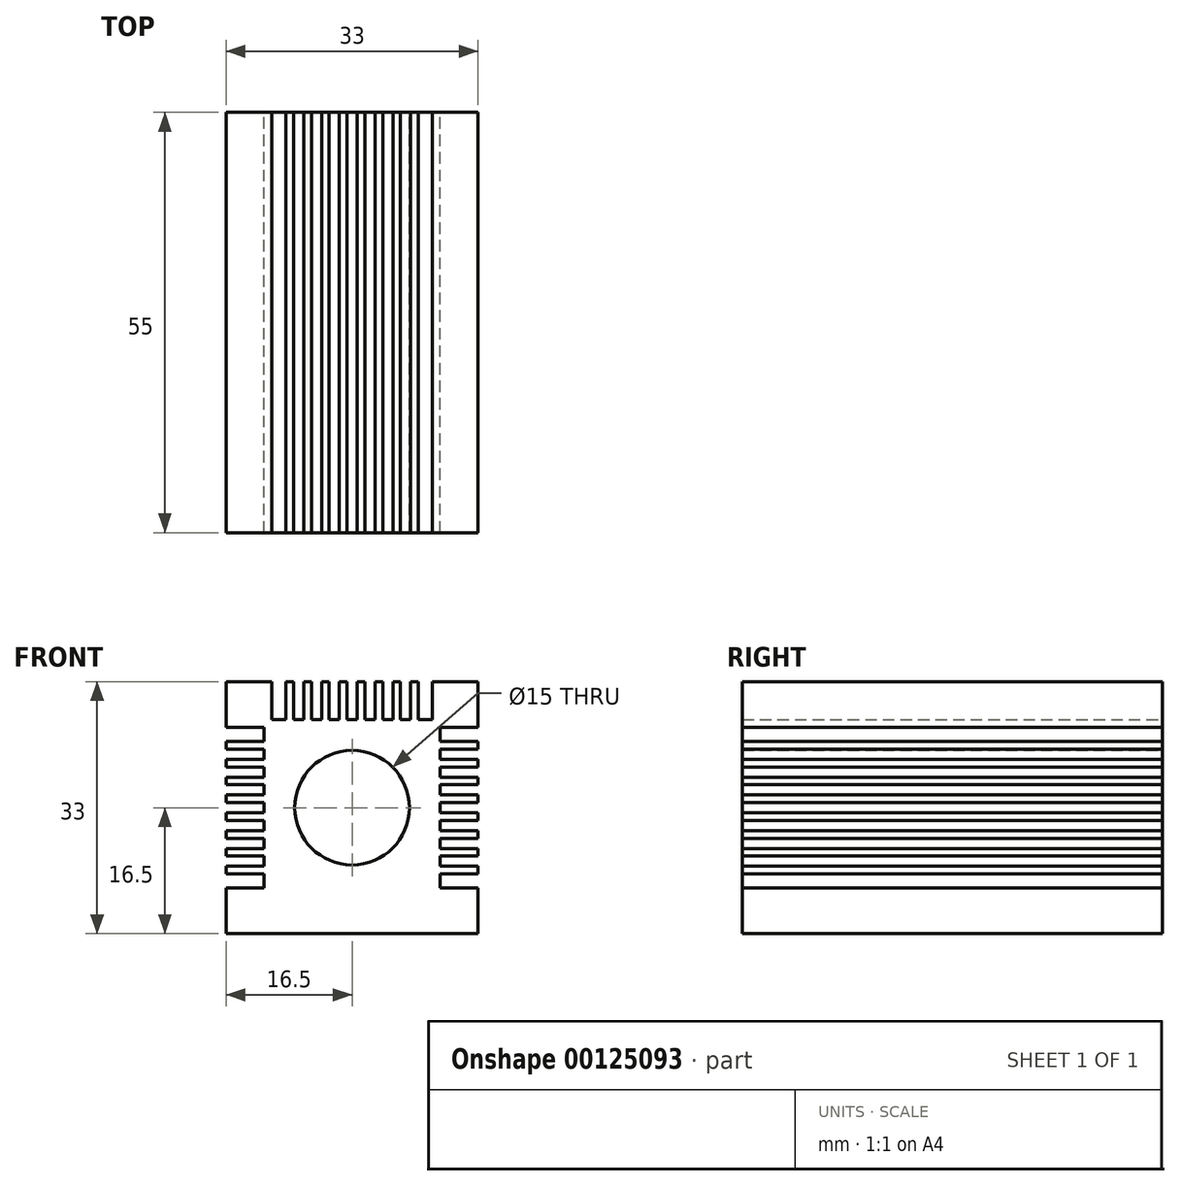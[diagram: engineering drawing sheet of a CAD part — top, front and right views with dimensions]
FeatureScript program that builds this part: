
annotation { "Feature Type Name" : "Feature", "Feature Type Description" : "" }
export const myFeature = defineFeature(function(context is Context, id is Id, definition is map)
    precondition{}
    {
        {
            var Q0;
            Q0=qCreatedBy(makeId("Front.planeOp"),FACE);
            var sketch = newSketch(context, id + "F0", { "sketchPlane" : qUnion([Q0])});
            skLineSegment(sketch, "E0.bottom", {"start": v(0, 0) * mm, "end": v(33, 0) * mm});
            skLineSegment(sketch, "E0.top", {"start": v(0, 33) * mm, "end": v(6, 33) * mm});
            skLineSegment(sketch, "E0.left", {"start": v(0, 0) * mm, "end": v(0, 6) * mm});
            skLineSegment(sketch, "E0.right", {"start": v(33, 0) * mm, "end": v(33, 6) * mm});
            skLineSegment(sketch, "E1", {"start": v(6, 33) * mm, "end": v(6, 28) * mm});
            skLineSegment(sketch, "E2.MirrorCS", {"start": v(27, 33) * mm, "end": v(27, 28) * mm});
            skLineSegment(sketch, "E3.MirrorCS", {"start": v(6, 28) * mm, "end": v(7.83, 28) * mm});
            skPoint(sketch, "E4.orphan", {"position": v(6, 0) * mm});
            skPoint(sketch, "E5.orphan", {"position": v(16.5, 0) * mm});
            skPoint(sketch, "E6.orphan", {"position": v(27, 0) * mm});
            skPoint(sketch, "E7.start.orphan", {"position": v(16.5, 33) * mm});
            skPoint(sketch, "E8.trimOffspring.end.orphan", {"position": v(33, 16.5) * mm});
            skPoint(sketch, "E9.start.orphan", {"position": v(0, 16.5) * mm});
            skLineSegment(sketch, "E10", {"start": v(7.83, 33) * mm, "end": v(7.83, 28) * mm});
            skLineSegment(sketch, "E11.MirrorCS", {"start": v(8.83, 33) * mm, "end": v(8.83, 28) * mm});
            skLineSegment(sketch, "E12.1.0.0", {"start": v(10.17, 33) * mm, "end": v(10.17, 28) * mm});
            skLineSegment(sketch, "E12.1.0.1", {"start": v(11.17, 33) * mm, "end": v(11.17, 28) * mm});
            skLineSegment(sketch, "E12.2.0.0", {"start": v(12.5, 33) * mm, "end": v(12.5, 28) * mm});
            skLineSegment(sketch, "E12.2.0.1", {"start": v(13.5, 33) * mm, "end": v(13.5, 28) * mm});
            skLineSegment(sketch, "E12.3.0.0", {"start": v(14.83, 33) * mm, "end": v(14.83, 28) * mm});
            skLineSegment(sketch, "E12.3.0.1", {"start": v(15.83, 33) * mm, "end": v(15.83, 28) * mm});
            skLineSegment(sketch, "E12.4.0.0", {"start": v(17.17, 33) * mm, "end": v(17.17, 28) * mm});
            skLineSegment(sketch, "E12.4.0.1", {"start": v(18.17, 33) * mm, "end": v(18.17, 28) * mm});
            skLineSegment(sketch, "E12.5.0.0", {"start": v(19.5, 33) * mm, "end": v(19.5, 28) * mm});
            skLineSegment(sketch, "E12.5.0.1", {"start": v(20.5, 33) * mm, "end": v(20.5, 28) * mm});
            skLineSegment(sketch, "E12.6.0.0", {"start": v(21.83, 33) * mm, "end": v(21.83, 28) * mm});
            skLineSegment(sketch, "E12.6.0.1", {"start": v(22.83, 33) * mm, "end": v(22.83, 28) * mm});
            skLineSegment(sketch, "E12.7.0.0", {"start": v(24.17, 33) * mm, "end": v(24.17, 28) * mm});
            skLineSegment(sketch, "E12.7.0.1", {"start": v(25.17, 33) * mm, "end": v(25.17, 28) * mm});
            skLineSegment(sketch, "E12.direction1", {"start": v(8.83, 28) * mm, "end": v(10.17, 28) * mm, "construction": true});
            skLineSegment(sketch, "E13.trimOffspring", {"start": v(7.83, 33) * mm, "end": v(8.83, 33) * mm});
            skLineSegment(sketch, "E14.trimOffspring", {"start": v(10.17, 33) * mm, "end": v(11.17, 33) * mm});
            skLineSegment(sketch, "E15.trimOffspring", {"start": v(12.5, 33) * mm, "end": v(13.5, 33) * mm});
            skLineSegment(sketch, "E16.trimOffspring", {"start": v(14.83, 33) * mm, "end": v(15.83, 33) * mm});
            skLineSegment(sketch, "E17.trimOffspring", {"start": v(17.17, 33) * mm, "end": v(18.17, 33) * mm});
            skLineSegment(sketch, "E18.trimOffspring", {"start": v(19.5, 33) * mm, "end": v(20.5, 33) * mm});
            skLineSegment(sketch, "E19.trimOffspring", {"start": v(21.83, 33) * mm, "end": v(22.83, 33) * mm});
            skLineSegment(sketch, "E20.trimOffspring", {"start": v(24.17, 33) * mm, "end": v(25.17, 33) * mm});
            skLineSegment(sketch, "E21.trimOffspring", {"start": v(27, 33) * mm, "end": v(33, 33) * mm});
            skLineSegment(sketch, "E22.MirrorCS", {"start": v(0, 18.17) * mm, "end": v(0, 17.17) * mm});
            skLineSegment(sketch, "E23.MirrorCS", {"start": v(0, 8.83) * mm, "end": v(0, 7.83) * mm});
            skLineSegment(sketch, "E24.MirrorCS", {"start": v(0, 22.83) * mm, "end": v(0, 21.83) * mm});
            skLineSegment(sketch, "E25.MirrorCS", {"start": v(0, 11.17) * mm, "end": v(0, 10.17) * mm});
            skLineSegment(sketch, "E26.MirrorCS", {"start": v(0, 13.5) * mm, "end": v(0, 12.5) * mm});
            skLineSegment(sketch, "E27.MirrorCS", {"start": v(0, 20.5) * mm, "end": v(0, 19.5) * mm});
            skLineSegment(sketch, "E28.MirrorCS", {"start": v(0, 25.17) * mm, "end": v(0, 24.17) * mm});
            skLineSegment(sketch, "E29.MirrorCS", {"start": v(0, 15.83) * mm, "end": v(0, 14.83) * mm});
            skLineSegment(sketch, "E30.MirrorCS", {"start": v(0, 6) * mm, "end": v(5, 6) * mm});
            skLineSegment(sketch, "E31.MirrorCS", {"start": v(0, 7.83) * mm, "end": v(5, 7.83) * mm});
            skLineSegment(sketch, "E32.MirrorCS", {"start": v(0, 27) * mm, "end": v(5, 27) * mm});
            skLineSegment(sketch, "E33.MirrorCS", {"start": v(0, 13.5) * mm, "end": v(5, 13.5) * mm});
            skLineSegment(sketch, "E34.MirrorCS", {"start": v(0, 18.17) * mm, "end": v(5, 18.17) * mm});
            skLineSegment(sketch, "E35.MirrorCS", {"start": v(0, 8.83) * mm, "end": v(5, 8.83) * mm});
            skLineSegment(sketch, "E36.MirrorCS", {"start": v(0, 21.83) * mm, "end": v(5, 21.83) * mm});
            skLineSegment(sketch, "E37.MirrorCS", {"start": v(0, 11.17) * mm, "end": v(5, 11.17) * mm});
            skLineSegment(sketch, "E38.MirrorCS", {"start": v(0, 22.83) * mm, "end": v(5, 22.83) * mm});
            skLineSegment(sketch, "E39.MirrorCS", {"start": v(0, 12.5) * mm, "end": v(5, 12.5) * mm});
            skLineSegment(sketch, "E40.MirrorCS", {"start": v(0, 15.83) * mm, "end": v(5, 15.83) * mm});
            skLineSegment(sketch, "E41.MirrorCS", {"start": v(0, 25.17) * mm, "end": v(5, 25.17) * mm});
            skLineSegment(sketch, "E42.MirrorCS", {"start": v(0, 20.5) * mm, "end": v(5, 20.5) * mm});
            skLineSegment(sketch, "E43.MirrorCS", {"start": v(0, 17.17) * mm, "end": v(5, 17.17) * mm});
            skLineSegment(sketch, "E44.MirrorCS", {"start": v(0, 19.5) * mm, "end": v(5, 19.5) * mm});
            skLineSegment(sketch, "E45.MirrorCS", {"start": v(0, 14.83) * mm, "end": v(5, 14.83) * mm});
            skLineSegment(sketch, "E46.MirrorCS", {"start": v(0, 24.17) * mm, "end": v(5, 24.17) * mm});
            skLineSegment(sketch, "E47.MirrorCS", {"start": v(0, 10.17) * mm, "end": v(5, 10.17) * mm});
            skLineSegment(sketch, "E48", {"start": v(5, 27) * mm, "end": v(5, 25.17) * mm});
            skLineSegment(sketch, "E49.trimOffspring", {"start": v(0, 27) * mm, "end": v(0, 33) * mm});
            skLineSegment(sketch, "E50.trimOffspring", {"start": v(0, 24.17) * mm, "end": v(0, 25.17) * mm});
            skLineSegment(sketch, "E51.trimOffspring", {"start": v(0, 21.83) * mm, "end": v(0, 22.83) * mm});
            skLineSegment(sketch, "E52.trimOffspring", {"start": v(0, 19.5) * mm, "end": v(0, 20.5) * mm});
            skLineSegment(sketch, "E53.trimOffspring", {"start": v(0, 7.83) * mm, "end": v(0, 8.83) * mm});
            skLineSegment(sketch, "E54.trimOffspring", {"start": v(0, 10.17) * mm, "end": v(0, 11.17) * mm});
            skLineSegment(sketch, "E55.trimOffspring", {"start": v(0, 12.5) * mm, "end": v(0, 13.5) * mm});
            skLineSegment(sketch, "E56.trimOffspring", {"start": v(0, 14.83) * mm, "end": v(0, 15.83) * mm});
            skLineSegment(sketch, "E57.trimOffspring", {"start": v(0, 17.17) * mm, "end": v(0, 18.17) * mm});
            skLineSegment(sketch, "E58.trimOffspring", {"start": v(25.17, 28) * mm, "end": v(27, 28) * mm});
            skLineSegment(sketch, "E59.trimOffspring", {"start": v(22.83, 28) * mm, "end": v(24.17, 28) * mm});
            skLineSegment(sketch, "E60.trimOffspring", {"start": v(20.5, 28) * mm, "end": v(21.83, 28) * mm});
            skLineSegment(sketch, "E61.trimOffspring", {"start": v(18.17, 28) * mm, "end": v(19.5, 28) * mm});
            skLineSegment(sketch, "E62.trimOffspring", {"start": v(15.83, 28) * mm, "end": v(17.17, 28) * mm});
            skLineSegment(sketch, "E63.trimOffspring", {"start": v(11.17, 28) * mm, "end": v(12.5, 28) * mm});
            skLineSegment(sketch, "E64.trimOffspring", {"start": v(8.83, 28) * mm, "end": v(10.17, 28) * mm});
            skLineSegment(sketch, "E65.trimOffspring", {"start": v(13.5, 28) * mm, "end": v(14.83, 28) * mm});
            skLineSegment(sketch, "E66.trimOffspring", {"start": v(5, 21.83) * mm, "end": v(5, 20.5) * mm});
            skLineSegment(sketch, "E67.trimOffspring", {"start": v(5, 24.17) * mm, "end": v(5, 22.83) * mm});
            skLineSegment(sketch, "E68.trimOffspring", {"start": v(5, 19.5) * mm, "end": v(5, 18.17) * mm});
            skLineSegment(sketch, "E69.trimOffspring", {"start": v(5, 10.17) * mm, "end": v(5, 8.83) * mm});
            skLineSegment(sketch, "E70.trimOffspring", {"start": v(5, 12.5) * mm, "end": v(5, 11.17) * mm});
            skLineSegment(sketch, "E71.trimOffspring", {"start": v(5, 7.83) * mm, "end": v(5, 6) * mm});
            skLineSegment(sketch, "E72.trimOffspring", {"start": v(5, 17.17) * mm, "end": v(5, 13.5) * mm});
            skLineSegment(sketch, "E73.MirrorCS", {"start": v(28, 8.83) * mm, "end": v(28, 10.17) * mm});
            skLineSegment(sketch, "E74.MirrorCS", {"start": v(28, 8.83) * mm, "end": v(28, 10.17) * mm, "construction": true});
            skLineSegment(sketch, "E75.MirrorCS", {"start": v(28, 18.17) * mm, "end": v(28, 19.5) * mm});
            skLineSegment(sketch, "E76.MirrorCS", {"start": v(28, 15.83) * mm, "end": v(28, 17.17) * mm});
            skLineSegment(sketch, "E77.MirrorCS", {"start": v(28, 11.17) * mm, "end": v(28, 12.5) * mm});
            skLineSegment(sketch, "E78.MirrorCS", {"start": v(33, 21.83) * mm, "end": v(33, 22.83) * mm});
            skLineSegment(sketch, "E79.MirrorCS", {"start": v(28, 25.17) * mm, "end": v(28, 27) * mm});
            skLineSegment(sketch, "E80.MirrorCS", {"start": v(33, 24.17) * mm, "end": v(33, 25.17) * mm});
            skLineSegment(sketch, "E81.MirrorCS", {"start": v(28, 6) * mm, "end": v(28, 7.83) * mm});
            skLineSegment(sketch, "E82.MirrorCS", {"start": v(33, 17.17) * mm, "end": v(33, 18.17) * mm});
            skLineSegment(sketch, "E83.MirrorCS", {"start": v(28, 20.5) * mm, "end": v(28, 21.83) * mm});
            skLineSegment(sketch, "E84.MirrorCS", {"start": v(33, 7.83) * mm, "end": v(33, 8.83) * mm});
            skLineSegment(sketch, "E85.MirrorCS", {"start": v(33, 12.5) * mm, "end": v(33, 13.5) * mm});
            skLineSegment(sketch, "E86.MirrorCS", {"start": v(28, 13.5) * mm, "end": v(28, 14.83) * mm});
            skLineSegment(sketch, "E87.MirrorCS", {"start": v(28, 22.83) * mm, "end": v(28, 24.17) * mm});
            skLineSegment(sketch, "E88.MirrorCS", {"start": v(33, 14.83) * mm, "end": v(33, 15.83) * mm});
            skLineSegment(sketch, "E89.MirrorCS", {"start": v(33, 10.17) * mm, "end": v(33, 11.17) * mm});
            skLineSegment(sketch, "E90.MirrorCS", {"start": v(33, 19.5) * mm, "end": v(33, 20.5) * mm});
            skLineSegment(sketch, "E91.MirrorCS", {"start": v(33, 20.5) * mm, "end": v(28, 20.5) * mm});
            skLineSegment(sketch, "E92.MirrorCS", {"start": v(33, 21.83) * mm, "end": v(28, 21.83) * mm});
            skLineSegment(sketch, "E93.MirrorCS", {"start": v(33, 19.5) * mm, "end": v(28, 19.5) * mm});
            skLineSegment(sketch, "E94.MirrorCS", {"start": v(33, 22.83) * mm, "end": v(28, 22.83) * mm});
            skLineSegment(sketch, "E95.MirrorCS", {"start": v(33, 24.17) * mm, "end": v(28, 24.17) * mm});
            skLineSegment(sketch, "E96.MirrorCS", {"start": v(33, 25.17) * mm, "end": v(28, 25.17) * mm});
            skLineSegment(sketch, "E97.MirrorCS", {"start": v(33, 14.83) * mm, "end": v(28, 14.83) * mm});
            skLineSegment(sketch, "E98.MirrorCS", {"start": v(33, 15.83) * mm, "end": v(28, 15.83) * mm});
            skLineSegment(sketch, "E99.MirrorCS", {"start": v(33, 17.17) * mm, "end": v(28, 17.17) * mm});
            skLineSegment(sketch, "E100.MirrorCS", {"start": v(33, 6) * mm, "end": v(28, 6) * mm});
            skLineSegment(sketch, "E101.MirrorCS", {"start": v(33, 27) * mm, "end": v(28, 27) * mm});
            skLineSegment(sketch, "E102.MirrorCS", {"start": v(33, 8.83) * mm, "end": v(28, 8.83) * mm});
            skLineSegment(sketch, "E103.MirrorCS", {"start": v(33, 10.17) * mm, "end": v(28, 10.17) * mm});
            skLineSegment(sketch, "E104.MirrorCS", {"start": v(33, 13.5) * mm, "end": v(28, 13.5) * mm});
            skLineSegment(sketch, "E105.MirrorCS", {"start": v(33, 11.17) * mm, "end": v(28, 11.17) * mm});
            skLineSegment(sketch, "E106.MirrorCS", {"start": v(33, 7.83) * mm, "end": v(28, 7.83) * mm});
            skLineSegment(sketch, "E107.MirrorCS", {"start": v(33, 18.17) * mm, "end": v(28, 18.17) * mm});
            skLineSegment(sketch, "E108.MirrorCS", {"start": v(33, 12.5) * mm, "end": v(28, 12.5) * mm});
            skLineSegment(sketch, "E109.trimOffspring", {"start": v(33, 27) * mm, "end": v(33, 33) * mm});
            skCircle(sketch, "E110", {"center": v(16.5, 16.5) * mm, "radius": 7.5 * mm});
            skSolve(sketch);
        }
        {
            var Q0;
            Q0 = qSketchRegion(id + "F0", true);
            extrude(context, id + "F1", {"entities" : qUnion([Q0]), "depth" : 55 * mm});
        }
    });
